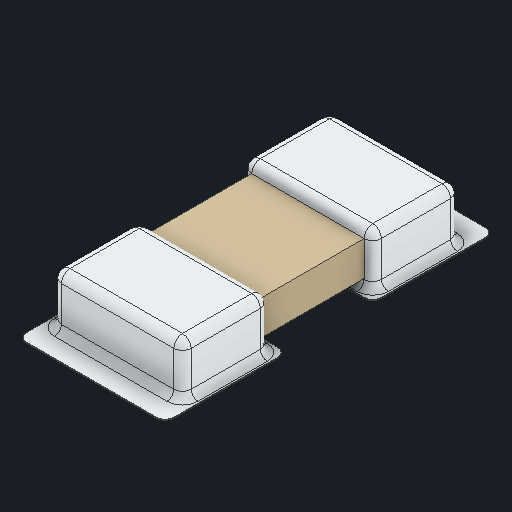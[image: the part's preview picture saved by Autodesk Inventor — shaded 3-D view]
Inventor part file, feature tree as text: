
AUTODESK INVENTOR PART (.ipt)
format: ipt  version: 2023 (Build 270158000, 158)  size: 168,960 bytes
history: native  units: in
note: dims shown in document units (in); Inventor stores cm internally (conversion verified against a paired STEP export)
features: fillet x1
ambient origin geometry x8: Origin, YZ Plane, XZ Plane, XY Plane, X Axis, Y Axis, Z Axis, Center Point
bodies: Solid1 (feature_tree)
feature tree (1):
  fillet  "Fillet2"  [1 undecoded]
note: 1 required parameter value undecoded (feature->parameter linkage not recoverable at this tier; creation-order binding heuristic only, values carry confidence <= 0.55)
